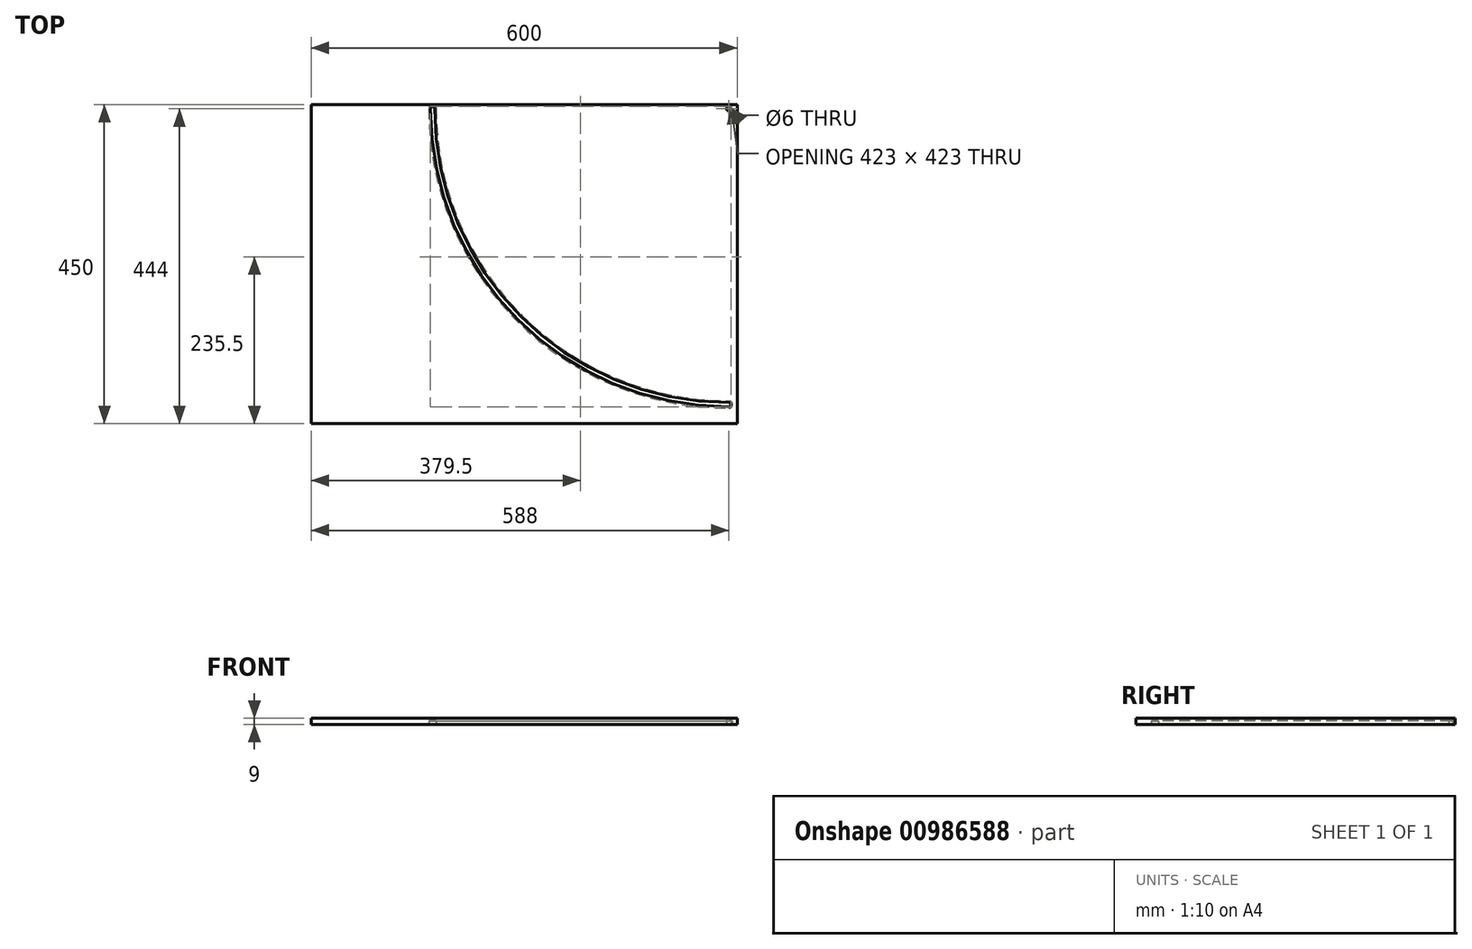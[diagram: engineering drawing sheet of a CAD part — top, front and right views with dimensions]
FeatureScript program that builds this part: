
annotation { "Feature Type Name" : "Feature", "Feature Type Description" : "" }
export const myFeature = defineFeature(function(context is Context, id is Id, definition is map)
    precondition{}
    {
        {
            var Q0;
            Q0=qCreatedBy(makeId("Top.planeOp"),FACE);
            var sketch = newSketch(context, id + "F0", { "sketchPlane" : qUnion([Q0])});
            skLineSegment(sketch, "E0.left", {"start": v(0, 0) * mm, "end": v(0, -450) * mm});
            skLineSegment(sketch, "E1.MirrorCS", {"start": v(0, 0) * mm, "end": v(-5.81, 0) * mm});
            skCircle(sketch, "E2.MirrorC", {"center": v(-12, -6) * mm, "radius": 3 * mm});
            skCircle(sketch, "E3.MirrorC", {"center": v(-12, -423) * mm, "radius": 3 * mm});
            skCircle(sketch, "E4.MirrorC", {"center": v(-429, -6) * mm, "radius": 3 * mm});
            skLineSegment(sketch, "E5.MirrorCS", {"start": v(0, -450) * mm, "end": v(-28.76, -450) * mm});
            skLineSegment(sketch, "E6.MirrorCS", {"start": v(-600, 0) * mm, "end": v(-600, -450) * mm});
            skLineSegment(sketch, "E7.MirrorCS", {"start": v(0, 0) * mm, "end": v(-600, 0) * mm});
            skLineSegment(sketch, "E8.MirrorCS", {"start": v(0, -450) * mm, "end": v(-600, -450) * mm});
            skArc(sketch, "E9", {"start": v(-432, -6) * mm, "mid": v(-308.98, -302.98) * mm, "end": v(-12, -426) * mm});
            skArc(sketch, "E10", {"start": v(-426, -6) * mm, "mid": v(-304.74, -298.74) * mm, "end": v(-12, -420) * mm});
            skSolve(sketch);
        }
        {
            var Q0;
            {var subQ0=sQuery(id+"F0.wireOp",EDGE,"E0.left");Q0=makeQuery(id+"F0.imprint","IMPRINT",FACE,{"disambiguationData":[TD([[makeQuery(id+"F0.imprint","IMPRINT",EDGE,{"derivedFrom":subQ0}),-1.0]])]});}
            extrude(context, id + "F1", {"entities" : qUnion([Q0]), "depth" : 9 * mm, "offsetDistance" : 25 * mm});
        }
        {
            var Q0;
            Q0=qCreatedBy(makeId("Top.planeOp"),FACE);
            var sketch = newSketch(context, id + "F2", { "sketchPlane" : qUnion([Q0])});
            skLineSegment(sketch, "E11.left", {"start": v(0, 0) * mm, "end": v(0.27, -449.15) * mm});
            skLineSegment(sketch, "E12.left", {"start": v(0.27, -449.15) * mm, "end": v(0.23, -415.68) * mm});
            skLineSegment(sketch, "E13.MirrorCS", {"start": v(0, 0) * mm, "end": v(-5.81, 0) * mm});
            skCircle(sketch, "E14.MirrorC", {"center": v(-12.26, -5.98) * mm, "radius": 3 * mm});
            skLineSegment(sketch, "E15.MirrorCS", {"start": v(0.27, -449.15) * mm, "end": v(0.27, -415.68) * mm});
            skLineSegment(sketch, "E16.MirrorCS", {"start": v(0.27, -449.15) * mm, "end": v(-28.49, -449.15) * mm});
            skLineSegment(sketch, "E17.MirrorCS", {"start": v(-600.26, 0.76) * mm, "end": v(-600.26, -449.15) * mm});
            skLineSegment(sketch, "E18.MirrorCS", {"start": v(0, 0) * mm, "end": v(-600.26, 0.76) * mm});
            skLineSegment(sketch, "E19.MirrorCS", {"start": v(0.27, -449.15) * mm, "end": v(-600.26, -449.15) * mm});
            skCircle(sketch, "E20", {"center": v(-429.26, -5.45) * mm, "radius": 5.2 * mm});
            skCircle(sketch, "E21", {"center": v(-11.73, -422.98) * mm, "radius": 5.2 * mm});
            skArc(sketch, "E22", {"start": v(-424.06, -5.46) * mm, "mid": v(-303.44, -297.17) * mm, "end": v(-11.73, -417.78) * mm});
            skArc(sketch, "E23", {"start": v(-434.46, -5.45) * mm, "mid": v(-310.8, -304.53) * mm, "end": v(-11.72, -428.18) * mm});
            skSolve(sketch);
        }
        {
            var Q0;
            {var subQ0=sQuery(id+"F2.wireOp",EDGE,"E22");Q0=makeQuery(id+"F2.imprint","IMPRINT",FACE,{"disambiguationData":[TD([[makeQuery(id+"F2.imprint","IMPRINT",EDGE,{"derivedFrom":subQ0}),-1.0]])]});}
            var Q1;
            {var subQ0=sQuery(id+"F2.wireOp",EDGE,"E20");var subQ1=makeQuery(id+"F2.imprint","INTERSECT",VERTEX,{"derivedFrom":[subQ0,sQuery(id+"F2.wireOp",EDGE,"E22")]});Q1=makeQuery(id+"F2.imprint","IMPRINT",FACE,{"disambiguationData":[TD([[makeQuery(id+"F2.imprint","IMPRINT",EDGE,{"disambiguationData":[TD([[subQ1,1.0]])],"derivedFrom":subQ0}),1.0]])]});}
            var Q2;
            {var subQ0=sQuery(id+"F2.wireOp",EDGE,"E21");var subQ1=makeQuery(id+"F2.imprint","INTERSECT",VERTEX,{"derivedFrom":[subQ0,sQuery(id+"F2.wireOp",EDGE,"E22")]});Q2=makeQuery(id+"F2.imprint","IMPRINT",FACE,{"disambiguationData":[TD([[makeQuery(id+"F2.imprint","IMPRINT",EDGE,{"disambiguationData":[TD([[subQ1,-1.0]])],"derivedFrom":subQ0}),1.0]])]});}
            extrude(context, id + "F3", {"entities" : qUnion([Q0, Q1, Q2]), "operationType" : NewBodyOperationType.REMOVE, "depth" : 5 * mm, "offsetDistance" : 25 * mm});
        }
    });
